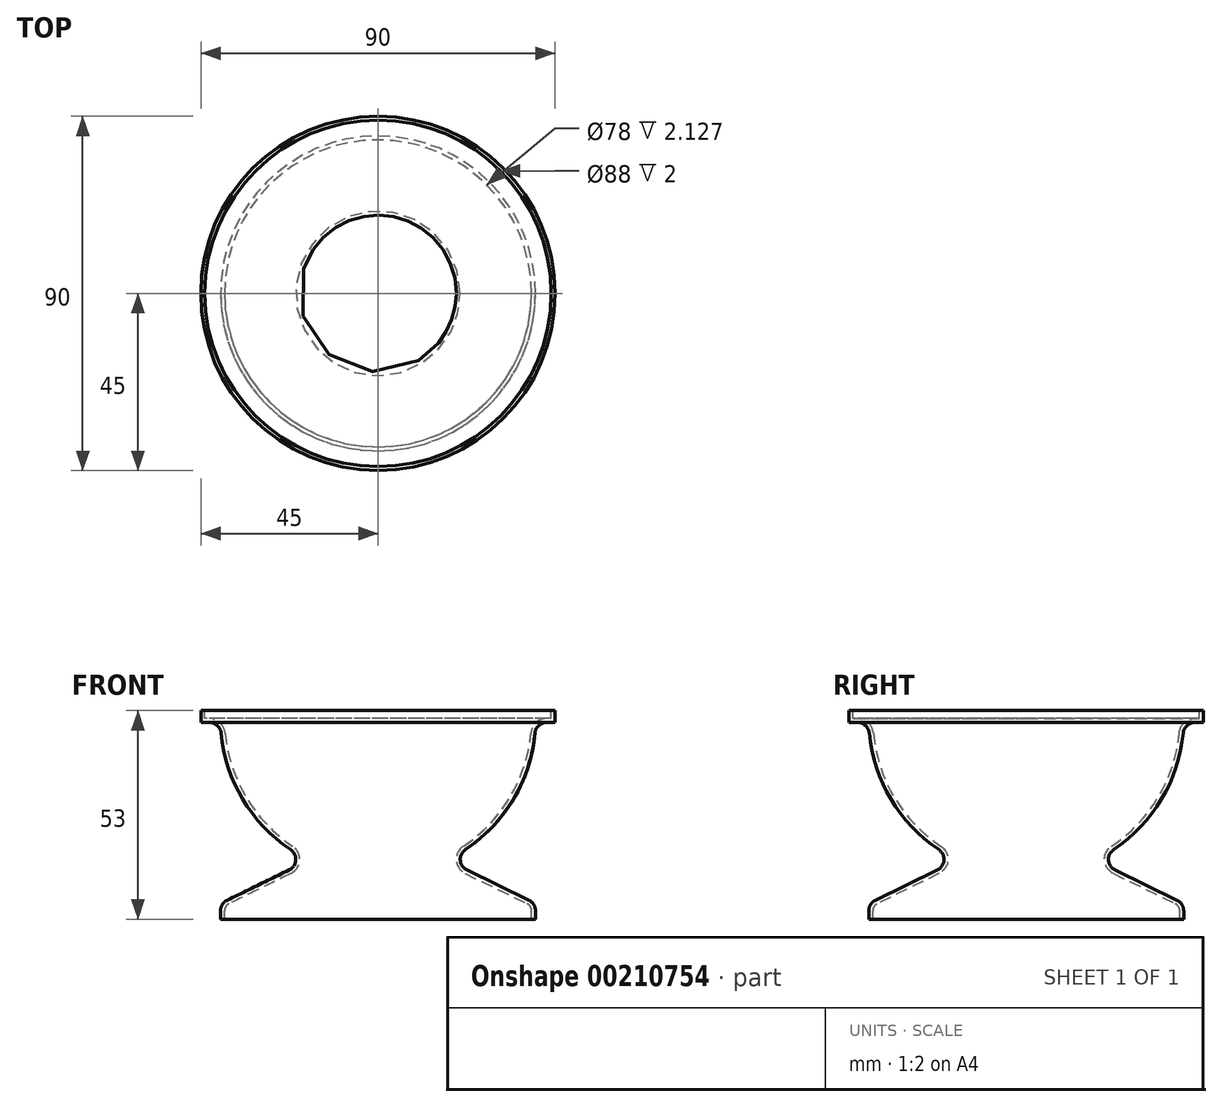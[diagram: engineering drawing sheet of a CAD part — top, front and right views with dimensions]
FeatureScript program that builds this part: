
annotation { "Feature Type Name" : "Feature", "Feature Type Description" : "" }
export const myFeature = defineFeature(function(context is Context, id is Id, definition is map)
    precondition{}
    {
        {
            var Q0;
            Q0=qCreatedBy(makeId("Front.planeOp"),FACE);
            var sketch = newSketch(context, id + "F0", { "sketchPlane" : qUnion([Q0])});
            skLineSegment(sketch, "E0", {"start": v(0, 0) * mm, "end": v(40, 0) * mm});
            skLineSegment(sketch, "E1", {"start": v(40, 4) * mm, "end": v(17.5, 15) * mm});
            skLineSegment(sketch, "E2", {"start": v(17.5, 15) * mm, "end": v(0, 15) * mm});
            skLineSegment(sketch, "E3", {"start": v(0, 15) * mm, "end": v(0, 0) * mm});
            skLineSegment(sketch, "E4", {"start": v(0, 15) * mm, "end": v(0, 53) * mm});
            skLineSegment(sketch, "E5", {"start": v(0, 53) * mm, "end": v(40, 53) * mm});
            skArc(sketch, "E6", {"start": v(17.5, 15) * mm, "mid": v(34.46, 30.62) * mm, "end": v(40, 53) * mm});
            skLineSegment(sketch, "E7", {"start": v(0, 79.72) * mm, "end": v(0, -10.85) * mm, "construction": true});
            skLineSegment(sketch, "E8", {"start": v(40, 4) * mm, "end": v(40, 0) * mm});
            skPoint(sketch, "E8.endSnap0", {"position": v(24.1, 0) * mm});
            skPoint(sketch, "E9.orphan", {"position": v(48.18, 0) * mm});
            skSolve(sketch);
        }
        {
            var Q0;
            Q0 = qSketchRegion(id + "F0", true);
            var Q1;
            Q1=sQuery(id+"F0.wireOp",EDGE,"E7");
            revolve(context, id + "F1", {"entities" : qUnion([Q0]), "axis" : qUnion([Q1]), "revolveType" : RevolveType.FULL});
        }
        {
            var Q0;
            Q0=makeQuery(id+"F1.opRevolve","SWEPT_FACE",FACE,{"disambiguationData":[OSD([sQuery(id+"F0.wireOp",EDGE,"E5")])]});
            var sketch = newSketch(context, id + "F2", { "sketchPlane" : qUnion([Q0])});
            skCircle(sketch, "E10", {"center": v(0, 0) * mm, "radius": 40 * mm});
            skCircle(sketch, "E11.0", {"center": v(0, 0) * mm, "radius": 37 * mm});
            skCircle(sketch, "E12.0", {"center": v(0, 0) * mm, "radius": 45 * mm});
            skSolve(sketch);
        }
        {
            var Q0;
            Q0 = qSketchRegion(id + "F2", true);
            extrude(context, id + "F3", {"entities" : qUnion([Q0]), "operationType" : NewBodyOperationType.ADD, "oppositeDirection" : true, "depth" : 3 * mm});
        }
        {
            var Q0;
            Q0=makeQuery(id+"F1.opRevolve","SWEPT_EDGE",EDGE,{"disambiguationData":[OSD([sQuery(id+"F0.wireOp",EDGE,"E1"),sQuery(id+"F0.wireOp",EDGE,"E8")])]});
            var Q1;
            Q1=makeQuery(id+"F1.opRevolve","SWEPT_FACE",FACE,{"disambiguationData":[OSD([sQuery(id+"F0.wireOp",EDGE,"E1")])]});
            var Q2;
            Q2=makeQuery(id+"F3.boolean.opBoolean","INTERSECT",EDGE,{"derivedFrom":[makeQuery(id+"F1.opRevolve","SWEPT_FACE",FACE,{"disambiguationData":[OSD([sQuery(id+"F0.wireOp",EDGE,"E6")])]}),makeQuery(id+"F3.opExtrude","CAP_FACE",FACE,{"disambiguationData":[OSD([sQuery(id+"F2.wireOp",EDGE,"E10"),sQuery(id+"F2.wireOp",EDGE,"E12.0")])],"isStart":false})]});
            fillet(context, id + "F4", {"entities" : qUnion([Q0, Q1, Q2]), "radius" : 3 * mm, "tangentPropagation" : true, "allowEdgeOverflow" : false});
        }
        {
            var Q0;
            Q0=makeQuery(id+"F1.opRevolve","SWEPT_FACE",FACE,{"disambiguationData":[OSD([sQuery(id+"F0.wireOp",EDGE,"E0")])]});
            var Q1;
            Q1=makeQuery(id+"F3.boolean.opBoolean","MERGE",FACE,{"derivedFrom":[makeQuery(id+"F1.opRevolve","SWEPT_FACE",FACE,{"disambiguationData":[OSD([sQuery(id+"F0.wireOp",EDGE,"E5")])]}),makeQuery(id+"F3.opExtrude","CAP_FACE",FACE,{"disambiguationData":[OSD([sQuery(id+"F2.wireOp",EDGE,"E10"),sQuery(id+"F2.wireOp",EDGE,"E12.0")])],"isStart":true})]});
            shell(context, id + "F5", {"entities" : qUnion([Q0, Q1]), "thickness" : 1 * mm});
        }
    });
